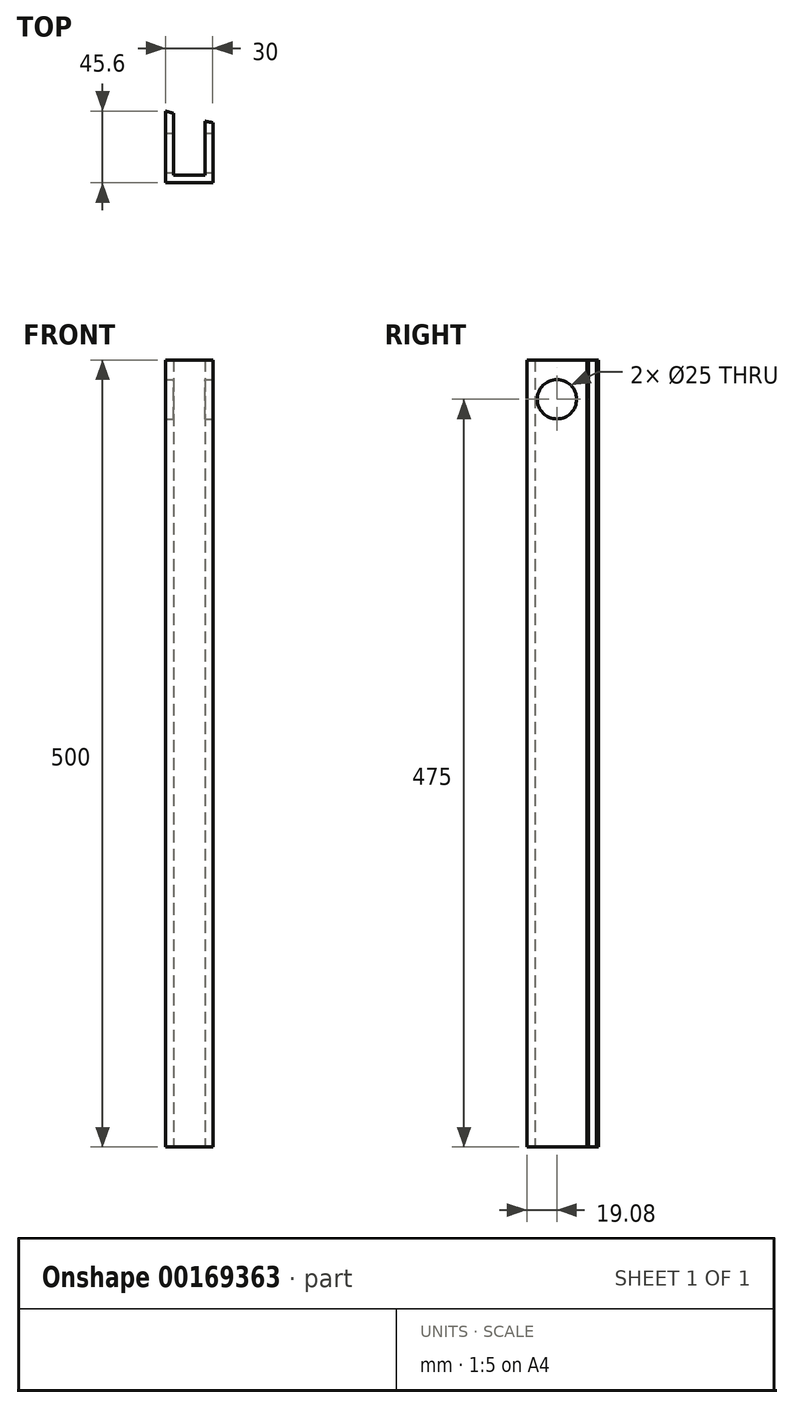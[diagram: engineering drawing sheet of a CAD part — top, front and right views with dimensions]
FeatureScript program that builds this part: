
annotation { "Feature Type Name" : "Feature", "Feature Type Description" : "" }
export const myFeature = defineFeature(function(context is Context, id is Id, definition is map)
    precondition{}
    {
        {
            var Q0;
            Q0=qCreatedBy(makeId("Top.planeOp"),FACE);
            var sketch = newSketch(context, id + "F0", { "sketchPlane" : qUnion([Q0])});
            skPoint(sketch, "E0", {"position": v(15, 21.57) * mm});
            skPoint(sketch, "E1", {"position": v(15, -16.6) * mm});
            skPoint(sketch, "E2", {"position": v(-15, -16.6) * mm});
            skPoint(sketch, "E3", {"position": v(-15, 29) * mm});
            skLineSegment(sketch, "E4", {"start": v(15, 21.57) * mm, "end": v(15, -16.6) * mm});
            skLineSegment(sketch, "E5", {"start": v(-15, -16.6) * mm, "end": v(-15, 29) * mm});
            skArc(sketch, "E6", {"start": v(-15, 29) * mm, "mid": v(-0.1, 24.85) * mm, "end": v(15, 21.57) * mm});
            skLineSegment(sketch, "E7", {"start": v(-15, -16.6) * mm, "end": v(15, -16.6) * mm});
            skPoint(sketch, "E8", {"position": v(-10, -16.6) * mm});
            skPoint(sketch, "E9", {"position": v(10, -16.6) * mm});
            skLineSegment(sketch, "E10", {"start": v(-10, -16.6) * mm, "end": v(-10, 27.5) * mm});
            skLineSegment(sketch, "E11", {"start": v(10, -16.6) * mm, "end": v(10, 22.56) * mm});
            skLineSegment(sketch, "E12", {"start": v(-10, 27.5) * mm, "end": v(10, 22.56) * mm});
            skPoint(sketch, "E13", {"position": v(-10, -11.6) * mm});
            skPoint(sketch, "E14", {"position": v(10, -11.6) * mm});
            skLineSegment(sketch, "E15", {"start": v(-10, -11.6) * mm, "end": v(10, -11.6) * mm});
            skSolve(sketch);
        }
        {
            var Q0;
            {var subQ4=sQuery(id+"F0.wireOp",EDGE,"E5");Q0=makeQuery(id+"F0.imprint","IMPRINT",FACE,{"disambiguationData":[TD([[makeQuery(id+"F0.imprint","IMPRINT",EDGE,{"derivedFrom":subQ4}),-1.0]])]});}
            var Q1;
            {var subQ5=sQuery(id+"F0.wireOp",EDGE,"E15");Q1=makeQuery(id+"F0.imprint","IMPRINT",FACE,{"disambiguationData":[TD([[makeQuery(id+"F0.imprint","IMPRINT",EDGE,{"derivedFrom":subQ5}),-1.0]])]});}
            var Q2;
            {var subQ4=sQuery(id+"F0.wireOp",EDGE,"E4");Q2=makeQuery(id+"F0.imprint","IMPRINT",FACE,{"disambiguationData":[TD([[makeQuery(id+"F0.imprint","IMPRINT",EDGE,{"derivedFrom":subQ4}),-1.0]])]});}
            extrude(context, id + "F1", {"entities" : qUnion([Q0, Q1, Q2]), "depth" : 500 * mm});
        }
        {
            var Q0;
            Q0=makeQuery(id+"F1.opExtrude","SWEPT_FACE",FACE,{"disambiguationData":[OSD([sQuery(id+"F0.wireOp",EDGE,"E4")])]});
            var sketch = newSketch(context, id + "F2", { "sketchPlane" : qUnion([Q0])});
            skPoint(sketch, "E16", {"position": v(-16.6, 500) * mm});
            skPoint(sketch, "E17", {"position": v(21.57, 500) * mm});
            skPoint(sketch, "E18", {"position": v(2.5, 500) * mm});
            skCircle(sketch, "E19", {"center": v(2.5, 475) * mm, "radius": 12.5 * mm});
            skSolve(sketch);
        }
        {
            var Q0;
            Q0=makeQuery(id+"F2.imprint","IMPRINT",FACE,{"disambiguationData":[TD([[makeQuery(id+"F2.imprint","IMPRINT",EDGE,{"derivedFrom":sQuery(id+"F2.wireOp",EDGE,"E19")}),1.0]])]});
            extrude(context, id + "F3", {"entities" : qUnion([Q0]), "operationType" : NewBodyOperationType.REMOVE, "oppositeDirection" : true, "depth" : 50 * mm});
        }
    });
